# Revit family: Котел_ТЕРМОТЕХНИК_ТТ150_ 1000-20000 кВт
name_source: partatom
category: Оборудование
units: mm (PartAtom-declared; Revit-internal decimal feet)

## family parameters
Всегда вертикально = Да
Классификация = Нет
На основе рабочей плоскости = Нет
Общий = Нет
При загрузке вырезать с полостями = Нет
Размер круглого соединителя = Использовать диаметр
Тип детали = Нормальный
Точка расчета площади = Нет

## types (23) — shared parameters
G = 25 мм
URL = https://www.entroros.ru
Видимость_ВКЛ = Да
Видимость_ВЫКЛ = Нет
Изготовитель = ЭНТРОРОС
Ключевая пометка = https://www.entroros.ru
Код по классификатору = D3020100
Материал_Условный BOX = <По категории>
Описание = Котел ЭНТРОРОС ТЕРМОТЕХНИК ТТ150
Производитель = ЭНТРОРОС
Семейство заказано = ООО ЭНТРОРОС (entroros.ru)
Семейство оборудования = ТТ150
Семейство разработано = ООО DASBIM (dasbim.ru)
Ссылка на документацию = https://www.entroros.ru
Штуцер_Датчик дым.газов_D = G1/2-B
Штуцер_Датчик темп. воды на входе_D = G1/2-B
Штуцер_Датчик темп. воды на выходе_D = G1/2-B
Штуцер_Слив воды_D = 40 мм
Штуцер_Слив конденсата_D = 25 мм
Штуцер_Слив конденсата_D_Формула = G1-B
Штуцер_Тягонапоромер_D = G1/2-B
Эксплуатационный КПД (%) не менее = 94
zero-valued in all types: Стоимость

## per-type parameters (varying)
- 01_1000_ef_306: B=1540 мм; H=1768 мм; L=3183 мм; А_Горелка=135 мм; А_Дверь_Смещение наружной грани=3038 мм; Аэродин. сопротивление (Па)=256; Дверь_052=Нет; Дверь_053=Нет; Дверь_054=Нет; Дверь_055=Нет; Дверь_151=Нет; Дверь_206=Да; Дверь_208=Нет; Дверь_210=Нет; Дверь_212=Нет; Дверь_213=Нет; Комментарии к типоразмеру=1000 кВт; Корпус_054=Нет; Корпус_151=Нет; Корпус_306=Да; Корпус_310=Нет; Корпус_311=Нет; Корпус_312=Нет; Корпус_313=Нет; Корпус_361=Нет; Корпус_362=Нет; Корпус_366=Нет; Корпус_367=Нет; Корпус_408=Нет; Корпус_409=Нет; Масса наполненного котла (кг)=5030; Масса сухого котла (кг)=3476; Ном. мощность (кВт)=1000; Подключение горелки=300; С_Ось котла=910 мм; Штуцер_Вход воды_D=125 мм; Штуцер_Вход воды_А=400 мм; Штуцер_Выход воды_D=125 мм; Штуцер_Выход воды_А=1038 мм; Штуцер_Выход дыма_D=350 мм; Штуцер_Выход дыма_В=1360 мм; Штуцер_Подключение горелки=300 мм; Штуцер_Пред.клапан1_А=430 мм; Штуцер_Пред.клапан2_А=300 мм; Штуцер_Пред.клапан_D=50 мм; Штуцер_Слив воды_D_Формула=G1/2-B; Штуцер_Слив воды_А=0 мм; Штуцер_Слив воды_В=86 мм; Штуцер_Слив конденсата_А=0 мм; Штуцер_Слив конденсата_В=231 мм
- 02_1500_ef_307: B=1540 мм; H=1768 мм; L=3183 мм; А_Горелка=135 мм; А_Дверь_Смещение наружной грани=3038 мм; Аэродин. сопротивление (Па)=673; Дверь_052=Нет; Дверь_053=Нет; Дверь_054=Нет; Дверь_055=Нет; Дверь_151=Нет; Дверь_206=Да; Дверь_208=Нет; Дверь_210=Нет; Дверь_212=Нет; Дверь_213=Нет; Комментарии к типоразмеру=1500 кВт; Корпус_054=Нет; Корпус_151=Нет; Корпус_306=Да; Корпус_310=Нет; Корпус_311=Нет; Корпус_312=Нет; Корпус_313=Нет; Корпус_361=Нет; Корпус_362=Нет; Корпус_366=Нет; Корпус_367=Нет; Корпус_408=Нет; Корпус_409=Нет; Масса наполненного котла (кг)=5163; Масса сухого котла (кг)=3547; Ном. мощность (кВт)=1500; Подключение горелки=300; С_Ось котла=910 мм; Штуцер_Вход воды_D=125 мм; Штуцер_Вход воды_А=400 мм; Штуцер_Выход воды_D=125 мм; Штуцер_Выход воды_А=1038 мм; Штуцер_Выход дыма_D=350 мм; Штуцер_Выход дыма_В=1360 мм; Штуцер_Подключение горелки=300 мм; Штуцер_Пред.клапан1_А=430 мм; Штуцер_Пред.клапан2_А=300 мм; Штуцер_Пред.клапан_D=50 мм; Штуцер_Слив воды_D_Формула=G1/2-B; Штуцер_Слив воды_А=0 мм; Штуцер_Слив воды_В=86 мм; Штуцер_Слив конденсата_А=0 мм; Штуцер_Слив конденсата_В=231 мм
- 03_2000_ef_308: B=1740 мм; H=1968 мм; L=3485 мм; А_Горелка=135 мм; А_Дверь_Смещение наружной грани=3340 мм; Аэродин. сопротивление (Па)=832; Дверь_052=Нет; Дверь_053=Нет; Дверь_054=Нет; Дверь_055=Нет; Дверь_151=Нет; Дверь_206=Нет; Дверь_208=Да; Дверь_210=Нет; Дверь_212=Нет; Дверь_213=Нет; Комментарии к типоразмеру=2000 кВт; Корпус_054=Нет; Корпус_151=Нет; Корпус_306=Нет; Корпус_310=Нет; Корпус_311=Нет; Корпус_312=Нет; Корпус_313=Нет; Корпус_361=Нет; Корпус_362=Нет; Корпус_366=Нет; Корпус_367=Нет; Корпус_408=Да; Корпус_409=Нет; Масса наполненного котла (кг)=7070; Масса сухого котла (кг)=4976; Ном. мощность (кВт)=2000; Подключение горелки=380; С_Ось котла=1010 мм; Штуцер_Вход воды_D=150 мм; Штуцер_Вход воды_А=550 мм; Штуцер_Выход воды_D=150 мм; Штуцер_Выход воды_А=820 мм; Штуцер_Выход дыма_D=500 мм; Штуцер_Выход дыма_В=1520 мм; Штуцер_Подключение горелки=380 мм; Штуцер_Пред.клапан1_А=1205 мм; Штуцер_Пред.клапан2_А=300 мм; Штуцер_Пред.клапан_D=65 мм; Штуцер_Слив воды_D_Формула=G1/2-B; Штуцер_Слив воды_А=0 мм; Штуцер_Слив воды_В=86 мм; Штуцер_Слив конденсата_А=0 мм; Штуцер_Слив конденсата_В=232 мм
- 04_2200_ef_3081: B=1740 мм; H=1968 мм; L=3485 мм; А_Горелка=135 мм; А_Дверь_Смещение наружной грани=3340 мм; Аэродин. сопротивление (Па)=1043; Дверь_052=Нет; Дверь_053=Нет; Дверь_054=Нет; Дверь_055=Нет; Дверь_151=Нет; Дверь_206=Нет; Дверь_208=Да; Дверь_210=Нет; Дверь_212=Нет; Дверь_213=Нет; Комментарии к типоразмеру=2200 кВт; Корпус_054=Нет; Корпус_151=Нет; Корпус_306=Нет; Корпус_310=Нет; Корпус_311=Нет; Корпус_312=Нет; Корпус_313=Нет; Корпус_361=Нет; Корпус_362=Нет; Корпус_366=Нет; Корпус_367=Нет; Корпус_408=Да; Корпус_409=Нет; Масса наполненного котла (кг)=7249; Масса сухого котла (кг)=5078; Ном. мощность (кВт)=2200; Подключение горелки=380; С_Ось котла=1010 мм; Штуцер_Вход воды_D=150 мм; Штуцер_Вход воды_А=550 мм; Штуцер_Выход воды_D=150 мм; Штуцер_Выход воды_А=820 мм; Штуцер_Выход дыма_D=500 мм; Штуцер_Выход дыма_В=1520 мм; Штуцер_Подключение горелки=380 мм; Штуцер_Пред.клапан1_А=1205 мм; Штуцер_Пред.клапан2_А=300 мм; Штуцер_Пред.клапан_D=65 мм; Штуцер_Слив воды_D_Формула=G1/2-B; Штуцер_Слив воды_А=0 мм; Штуцер_Слив воды_В=86 мм; Штуцер_Слив конденсата_А=0 мм; Штуцер_Слив конденсата_В=232 мм
- 05_2500_ef_309: B=1740 мм; H=1968 мм; L=3735 мм; А_Горелка=135 мм; А_Дверь_Смещение наружной грани=3590 мм; Аэродин. сопротивление (Па)=1032; Дверь_052=Нет; Дверь_053=Нет; Дверь_054=Нет; Дверь_055=Нет; Дверь_151=Нет; Дверь_206=Нет; Дверь_208=Да; Дверь_210=Нет; Дверь_212=Нет; Дверь_213=Нет; Комментарии к типоразмеру=2500 кВт; Корпус_054=Нет; Корпус_151=Нет; Корпус_306=Нет; Корпус_310=Нет; Корпус_311=Нет; Корпус_312=Нет; Корпус_313=Нет; Корпус_361=Нет; Корпус_362=Нет; Корпус_366=Нет; Корпус_367=Нет; Корпус_408=Нет; Корпус_409=Да; Масса наполненного котла (кг)=7796; Масса сухого котла (кг)=5571; Ном. мощность (кВт)=2500; Подключение горелки=380; С_Ось котла=1010 мм; Штуцер_Вход воды_D=150 мм; Штуцер_Вход воды_А=550 мм; Штуцер_Выход воды_D=150 мм; Штуцер_Выход воды_А=875 мм; Штуцер_Выход дыма_D=500 мм; Штуцер_Выход дыма_В=1520 мм; Штуцер_Подключение горелки=380 мм; Штуцер_Пред.клапан1_А=1400 мм; Штуцер_Пред.клапан2_А=300 мм; Штуцер_Пред.клапан_D=65 мм; Штуцер_Слив воды_D_Формула=G1/2-B; Штуцер_Слив воды_А=0 мм; Штуцер_Слив воды_В=89 мм; Штуцер_Слив конденсата_А=0 мм; Штуцер_Слив конденсата_В=233 мм
- 06_3000_ef_310: B=1940 мм; H=2168 мм; L=4123 мм; А_Горелка=135 мм; А_Дверь_Смещение наружной грани=3978 мм; Аэродин. сопротивление (Па)=898; Дверь_052=Нет; Дверь_053=Нет; Дверь_054=Нет; Дверь_055=Нет; Дверь_151=Нет; Дверь_206=Нет; Дверь_208=Нет; Дверь_210=Да; Дверь_212=Нет; Дверь_213=Нет; Комментарии к типоразмеру=3000 кВт; Корпус_054=Нет; Корпус_151=Нет; Корпус_306=Нет; Корпус_310=Да; Корпус_311=Нет; Корпус_312=Нет; Корпус_313=Нет; Корпус_361=Нет; Корпус_362=Нет; Корпус_366=Нет; Корпус_367=Нет; Корпус_408=Нет; Корпус_409=Нет; Масса наполненного котла (кг)=10357; Масса сухого котла (кг)=7423; Ном. мощность (кВт)=3000; Подключение горелки=450; С_Ось котла=1110 мм; Штуцер_Вход воды_D=200 мм; Штуцер_Вход воды_А=600 мм; Штуцер_Выход воды_D=200 мм; Штуцер_Выход воды_А=963 мм; Штуцер_Выход дыма_D=500 мм; Штуцер_Выход дыма_В=1720 мм; Штуцер_Подключение горелки=450 мм; Штуцер_Пред.клапан1_А=1600 мм; Штуцер_Пред.клапан2_А=300 мм; Штуцер_Пред.клапан_D=65 мм; Штуцер_Слив воды_D_Формула=G1/2-B; Штуцер_Слив воды_А=0 мм; Штуцер_Слив воды_В=86 мм; Штуцер_Слив конденсата_А=0 мм; Штуцер_Слив конденсата_В=233 мм
- 07_3200_ef_3101: B=1940 мм; H=2168 мм; L=4123 мм; А_Горелка=135 мм; А_Дверь_Смещение наружной грани=3978 мм; Аэродин. сопротивление (Па)=1046; Дверь_052=Нет; Дверь_053=Нет; Дверь_054=Нет; Дверь_055=Нет; Дверь_151=Нет; Дверь_206=Нет; Дверь_208=Нет; Дверь_210=Да; Дверь_212=Нет; Дверь_213=Нет; Комментарии к типоразмеру=3200 кВт; Корпус_054=Нет; Корпус_151=Нет; Корпус_306=Нет; Корпус_310=Да; Корпус_311=Нет; Корпус_312=Нет; Корпус_313=Нет; Корпус_361=Нет; Корпус_362=Нет; Корпус_366=Нет; Корпус_367=Нет; Корпус_408=Нет; Корпус_409=Нет; Масса наполненного котла (кг)=10625; Масса сухого котла (кг)=7575; Ном. мощность (кВт)=3200; Подключение горелки=450; С_Ось котла=1110 мм; Штуцер_Вход воды_D=200 мм; Штуцер_Вход воды_А=600 мм; Штуцер_Выход воды_D=200 мм; Штуцер_Выход воды_А=963 мм; Штуцер_Выход дыма_D=500 мм; Штуцер_Выход дыма_В=1720 мм; Штуцер_Подключение горелки=450 мм; Штуцер_Пред.клапан1_А=1600 мм; Штуцер_Пред.клапан2_А=300 мм; Штуцер_Пред.клапан_D=65 мм; Штуцер_Слив воды_D_Формула=G1/2-B; Штуцер_Слив воды_А=0 мм; Штуцер_Слив воды_В=86 мм; Штуцер_Слив конденсата_А=0 мм; Штуцер_Слив конденсата_В=233 мм
- 08_3500_ef_311: B=1940 мм; H=2168 мм; L=4523 мм; А_Горелка=135 мм; А_Дверь_Смещение наружной грани=4378 мм; Аэродин. сопротивление (Па)=1245; Дверь_052=Нет; Дверь_053=Нет; Дверь_054=Нет; Дверь_055=Нет; Дверь_151=Нет; Дверь_206=Нет; Дверь_208=Нет; Дверь_210=Да; Дверь_212=Нет; Дверь_213=Нет; Комментарии к типоразмеру=3500 кВт; Корпус_054=Нет; Корпус_151=Нет; Корпус_306=Нет; Корпус_310=Нет; Корпус_311=Да; Корпус_312=Нет; Корпус_313=Нет; Корпус_361=Нет; Корпус_362=Нет; Корпус_366=Нет; Корпус_367=Нет; Корпус_408=Нет; Корпус_409=Нет; Масса наполненного котла (кг)=11714; Масса сухого котла (кг)=8246; Ном. мощность (кВт)=3500; Подключение горелки=450; С_Ось котла=1110 мм; Штуцер_Вход воды_D=200 мм; Штуцер_Вход воды_А=600 мм; Штуцер_Выход воды_D=200 мм; Штуцер_Выход воды_А=1013 мм; Штуцер_Выход дыма_D=500 мм; Штуцер_Выход дыма_В=1720 мм; Штуцер_Подключение горелки=450 мм; Штуцер_Пред.клапан1_А=1950 мм; Штуцер_Пред.клапан2_А=300 мм; Штуцер_Пред.клапан_D=65 мм; Штуцер_Слив воды_D_Формула=G1/2-B; Штуцер_Слив воды_А=0 мм; Штуцер_Слив воды_В=86 мм; Штуцер_Слив конденсата_А=0 мм; Штуцер_Слив конденсата_В=233 мм
- 09_4200_ef_312: B=2100 мм; H=2326 мм; L=4820 мм; А_Горелка=135 мм; А_Дверь_Смещение наружной грани=4675 мм; Аэродин. сопротивление (Па)=1213; Дверь_052=Нет; Дверь_053=Нет; Дверь_054=Нет; Дверь_055=Нет; Дверь_151=Нет; Дверь_206=Нет; Дверь_208=Нет; Дверь_210=Нет; Дверь_212=Да; Дверь_213=Нет; Комментарии к типоразмеру=4200 кВт; Корпус_054=Нет; Корпус_151=Нет; Корпус_306=Нет; Корпус_310=Нет; Корпус_311=Нет; Корпус_312=Да; Корпус_313=Нет; Корпус_361=Нет; Корпус_362=Нет; Корпус_366=Нет; Корпус_367=Нет; Корпус_408=Нет; Корпус_409=Нет; Масса наполненного котла (кг)=14037; Масса сухого котла (кг)=10222; Ном. мощность (кВт)=4200; Подключение горелки=450; С_Ось котла=1205 мм; Штуцер_Вход воды_D=200 мм; Штуцер_Вход воды_А=700 мм; Штуцер_Выход воды_D=200 мм; Штуцер_Выход воды_А=960 мм; Штуцер_Выход дыма_D=650 мм; Штуцер_Выход дыма_В=1805 мм; Штуцер_Подключение горелки=450 мм; Штуцер_Пред.клапан1_А=2100 мм; Штуцер_Пред.клапан2_А=300 мм; Штуцер_Пред.клапан_D=80 мм; Штуцер_Слив воды_D_Формула=G1/2-B; Штуцер_Слив воды_А=0 мм; Штуцер_Слив воды_В=121 мм; Штуцер_Слив конденсата_А=0 мм; Штуцер_Слив конденсата_В=265 мм
- 10_5000_ef_3121: B=2100 мм; H=2326 мм; L=4820 мм; А_Горелка=135 мм; А_Дверь_Смещение наружной грани=4675 мм; Аэродин. сопротивление (Па)=1806; Дверь_052=Нет; Дверь_053=Нет; Дверь_054=Нет; Дверь_055=Нет; Дверь_151=Нет; Дверь_206=Нет; Дверь_208=Нет; Дверь_210=Нет; Дверь_212=Да; Дверь_213=Нет; Комментарии к типоразмеру=5000 кВт; Корпус_054=Нет; Корпус_151=Нет; Корпус_306=Нет; Корпус_310=Нет; Корпус_311=Нет; Корпус_312=Да; Корпус_313=Нет; Корпус_361=Нет; Корпус_362=Нет; Корпус_366=Нет; Корпус_367=Нет; Корпус_408=Нет; Корпус_409=Нет; Масса наполненного котла (кг)=14405; Масса сухого котла (кг)=10431; Ном. мощность (кВт)=5000; Подключение горелки=450; С_Ось котла=1205 мм; Штуцер_Вход воды_D=200 мм; Штуцер_Вход воды_А=700 мм; Штуцер_Выход воды_D=200 мм; Штуцер_Выход воды_А=960 мм; Штуцер_Выход дыма_D=650 мм; Штуцер_Выход дыма_В=1805 мм; Штуцер_Подключение горелки=450 мм; Штуцер_Пред.клапан1_А=2100 мм; Штуцер_Пред.клапан2_А=300 мм; Штуцер_Пред.клапан_D=80 мм; Штуцер_Слив воды_D_Формула=G1/2-B; Штуцер_Слив воды_А=0 мм; Штуцер_Слив воды_В=121 мм; Штуцер_Слив конденсата_А=0 мм; Штуцер_Слив конденсата_В=265 мм
- 11_5400_ef_313: B=2200 мм; H=2436 мм; L=5109 мм; А_Горелка=135 мм; А_Дверь_Смещение наружной грани=4964 мм; Аэродин. сопротивление (Па)=1059; Дверь_052=Нет; Дверь_053=Нет; Дверь_054=Нет; Дверь_055=Нет; Дверь_151=Нет; Дверь_206=Нет; Дверь_208=Нет; Дверь_210=Нет; Дверь_212=Нет; Дверь_213=Да; Комментарии к типоразмеру=5400 кВт; Корпус_054=Нет; Корпус_151=Нет; Корпус_306=Нет; Корпус_310=Нет; Корпус_311=Нет; Корпус_312=Нет; Корпус_313=Да; Корпус_361=Нет; Корпус_362=Нет; Корпус_366=Нет; Корпус_367=Нет; Корпус_408=Нет; Корпус_409=Нет; Масса наполненного котла (кг)=16565; Масса сухого котла (кг)=11363; Ном. мощность (кВт)=5400; Подключение горелки=450; С_Ось котла=1260 мм; Штуцер_Вход воды_D=250 мм; Штуцер_Вход воды_А=800 мм; Штуцер_Выход воды_D=250 мм; Штуцер_Выход воды_А=1147 мм; Штуцер_Выход дыма_D=650 мм; Штуцер_Выход дыма_В=1888 мм; Штуцер_Подключение горелки=450 мм; Штуцер_Пред.клапан1_А=2100 мм; Штуцер_Пред.клапан2_А=300 мм; Штуцер_Пред.клапан_D=80 мм; Штуцер_Слив воды_D_Формула=G1/2-B; Штуцер_Слив воды_А=0 мм; Штуцер_Слив воды_В=139 мм; Штуцер_Слив конденсата_А=0 мм; Штуцер_Слив конденсата_В=261 мм
- 12_6000_ef_3131: B=2200 мм; H=2436 мм; L=5109 мм; А_Горелка=135 мм; А_Дверь_Смещение наружной грани=4964 мм; Аэродин. сопротивление (Па)=1353; Дверь_052=Нет; Дверь_053=Нет; Дверь_054=Нет; Дверь_055=Нет; Дверь_151=Нет; Дверь_206=Нет; Дверь_208=Нет; Дверь_210=Нет; Дверь_212=Нет; Дверь_213=Да; Комментарии к типоразмеру=6000 кВт; Корпус_054=Нет; Корпус_151=Нет; Корпус_306=Нет; Корпус_310=Нет; Корпус_311=Нет; Корпус_312=Нет; Корпус_313=Да; Корпус_361=Нет; Корпус_362=Нет; Корпус_366=Нет; Корпус_367=Нет; Корпус_408=Нет; Корпус_409=Нет; Масса наполненного котла (кг)=16999; Масса сухого котла (кг)=11595; Ном. мощность (кВт)=6000; Подключение горелки=450; С_Ось котла=1260 мм; Штуцер_Вход воды_D=250 мм; Штуцер_Вход воды_А=800 мм; Штуцер_Выход воды_D=250 мм; Штуцер_Выход воды_А=1147 мм; Штуцер_Выход дыма_D=650 мм; Штуцер_Выход дыма_В=1888 мм; Штуцер_Подключение горелки=450 мм; Штуцер_Пред.клапан1_А=2100 мм; Штуцер_Пред.клапан2_А=300 мм; Штуцер_Пред.клапан_D=80 мм; Штуцер_Слив воды_D_Формула=50; Штуцер_Слив воды_А=0 мм; Штуцер_Слив воды_В=139 мм; Штуцер_Слив конденсата_А=0 мм; Штуцер_Слив конденсата_В=261 мм
- 13_6500_ef_151: B=2352 мм; H=2576 мм; L=5394 мм; А_Горелка=135 мм; А_Дверь_Смещение наружной грани=5249 мм; Аэродин. сопротивление (Па)=1126; Дверь_052=Нет; Дверь_053=Нет; Дверь_054=Нет; Дверь_055=Нет; Дверь_151=Да; Дверь_206=Нет; Дверь_208=Нет; Дверь_210=Нет; Дверь_212=Нет; Дверь_213=Нет; Комментарии к типоразмеру=6500 кВт; Корпус_054=Нет; Корпус_151=Да; Корпус_306=Нет; Корпус_310=Нет; Корпус_311=Нет; Корпус_312=Нет; Корпус_313=Нет; Корпус_361=Нет; Корпус_362=Нет; Корпус_366=Нет; Корпус_367=Нет; Корпус_408=Нет; Корпус_409=Нет; Масса наполненного котла (кг)=20128; Масса сухого котла (кг)=14706; Ном. мощность (кВт)=6500; Подключение горелки=500; С_Ось котла=1314 мм; Штуцер_Вход воды_D=250 мм; Штуцер_Вход воды_А=900 мм; Штуцер_Выход воды_D=250 мм; Штуцер_Выход воды_А=1134 мм; Штуцер_Выход дыма_D=800 мм; Штуцер_Выход дыма_В=1970 мм; Штуцер_Подключение горелки=500 мм; Штуцер_Пред.клапан1_А=1970 мм; Штуцер_Пред.клапан2_А=470 мм; Штуцер_Пред.клапан_D=100 мм; Штуцер_Слив воды_D_Формула=50; Штуцер_Слив воды_А=0 мм; Штуцер_Слив воды_В=110 мм; Штуцер_Слив конденсата_А=0 мм; Штуцер_Слив конденсата_В=237 мм
- 14_7000_ef_1511: B=2352 мм; H=2576 мм; L=5394 мм; А_Горелка=135 мм; А_Дверь_Смещение наружной грани=5249 мм; Аэродин. сопротивление (Па)=1339; Дверь_052=Нет; Дверь_053=Нет; Дверь_054=Нет; Дверь_055=Нет; Дверь_151=Да; Дверь_206=Нет; Дверь_208=Нет; Дверь_210=Нет; Дверь_212=Нет; Дверь_213=Нет; Комментарии к типоразмеру=7000 кВт; Корпус_054=Нет; Корпус_151=Да; Корпус_306=Нет; Корпус_310=Нет; Корпус_311=Нет; Корпус_312=Нет; Корпус_313=Нет; Корпус_361=Нет; Корпус_362=Нет; Корпус_366=Нет; Корпус_367=Нет; Корпус_408=Нет; Корпус_409=Нет; Масса наполненного котла (кг)=20671; Масса сухого котла (кг)=15007; Ном. мощность (кВт)=7000; Подключение горелки=500; С_Ось котла=1314 мм; Штуцер_Вход воды_D=250 мм; Штуцер_Вход воды_А=900 мм; Штуцер_Выход воды_D=250 мм; Штуцер_Выход воды_А=1134 мм; Штуцер_Выход дыма_D=800 мм; Штуцер_Выход дыма_В=1790 мм; Штуцер_Подключение горелки=500 мм; Штуцер_Пред.клапан1_А=1970 мм; Штуцер_Пред.клапан2_А=470 мм; Штуцер_Пред.клапан_D=100 мм; Штуцер_Слив воды_D_Формула=50; Штуцер_Слив воды_А=0 мм; Штуцер_Слив воды_В=110 мм; Штуцер_Слив конденсата_А=0 мм; Штуцер_Слив конденсата_В=237 мм
- 15_8000_ef_361: B=2500 мм; H=2710 мм; L=5806 мм; А_Горелка=148 мм; А_Дверь_Смещение наружной грани=5648 мм; Аэродин. сопротивление (Па)=1255; Дверь_052=Да; Дверь_053=Нет; Дверь_054=Нет; Дверь_055=Нет; Дверь_151=Нет; Дверь_206=Нет; Дверь_208=Нет; Дверь_210=Нет; Дверь_212=Нет; Дверь_213=Нет; Комментарии к типоразмеру=8000 кВт; Корпус_054=Нет; Корпус_151=Нет; Корпус_306=Нет; Корпус_310=Нет; Корпус_311=Нет; Корпус_312=Нет; Корпус_313=Нет; Корпус_361=Да; Корпус_362=Нет; Корпус_366=Нет; Корпус_367=Нет; Корпус_408=Нет; Корпус_409=Нет; Масса наполненного котла (кг)=24720; Масса сухого котла (кг)=17727; Ном. мощность (кВт)=8000; Подключение горелки=590; С_Ось котла=1370 мм; Штуцер_Вход воды_D=300 мм; Штуцер_Вход воды_А=1000 мм; Штуцер_Выход воды_D=300 мм; Штуцер_Выход воды_А=1216 мм; Штуцер_Выход дыма_D=800 мм; Штуцер_Выход дыма_В=2070 мм; Штуцер_Подключение горелки=590 мм; Штуцер_Пред.клапан1_А=1990 мм; Штуцер_Пред.клапан2_А=500 мм; Штуцер_Пред.клапан_D=100 мм; Штуцер_Слив воды_D_Формула=50; Штуцер_Слив воды_А=0 мм; Штуцер_Слив воды_В=99 мм; Штуцер_Слив конденсата_А=0 мм; Штуцер_Слив конденсата_В=213 мм
- 16_8700_ef_3611: B=2500 мм; H=2710 мм; L=5806 мм; А_Горелка=148 мм; А_Дверь_Смещение наружной грани=5648 мм; Аэродин. сопротивление (Па)=1524; Дверь_052=Да; Дверь_053=Нет; Дверь_054=Нет; Дверь_055=Нет; Дверь_151=Нет; Дверь_206=Нет; Дверь_208=Нет; Дверь_210=Нет; Дверь_212=Нет; Дверь_213=Нет; Комментарии к типоразмеру=8700 кВт; Корпус_054=Нет; Корпус_151=Нет; Корпус_306=Нет; Корпус_310=Нет; Корпус_311=Нет; Корпус_312=Нет; Корпус_313=Нет; Корпус_361=Да; Корпус_362=Нет; Корпус_366=Нет; Корпус_367=Нет; Корпус_408=Нет; Корпус_409=Нет; Масса наполненного котла (кг)=25373; Масса сухого котла (кг)=18089; Ном. мощность (кВт)=8700; Подключение горелки=590; С_Ось котла=1370 мм; Штуцер_Вход воды_D=300 мм; Штуцер_Вход воды_А=1000 мм; Штуцер_Выход воды_D=300 мм; Штуцер_Выход воды_А=1216 мм; Штуцер_Выход дыма_D=800 мм; Штуцер_Выход дыма_В=2070 мм; Штуцер_Подключение горелки=590 мм; Штуцер_Пред.клапан1_А=1990 мм; Штуцер_Пред.клапан2_А=500 мм; Штуцер_Пред.клапан_D=100 мм; Штуцер_Слив воды_D_Формула=50; Штуцер_Слив воды_А=0 мм; Штуцер_Слив воды_В=99 мм; Штуцер_Слив конденсата_А=0 мм; Штуцер_Слив конденсата_В=213 мм
- 17_10000_ef_362: B=2680 мм; H=2862 мм; L=6442 мм; А_Горелка=142 мм; А_Дверь_Смещение наружной грани=6290 мм; Аэродин. сопротивление (Па)=1458; Дверь_052=Нет; Дверь_053=Да; Дверь_054=Нет; Дверь_055=Нет; Дверь_151=Нет; Дверь_206=Нет; Дверь_208=Нет; Дверь_210=Нет; Дверь_212=Нет; Дверь_213=Нет; Комментарии к типоразмеру=10000 кВт; Корпус_054=Нет; Корпус_151=Нет; Корпус_306=Нет; Корпус_310=Нет; Корпус_311=Нет; Корпус_312=Нет; Корпус_313=Нет; Корпус_361=Нет; Корпус_362=Да; Корпус_366=Нет; Корпус_367=Нет; Корпус_408=Нет; Корпус_409=Нет; Масса наполненного котла (кг)=30251; Масса сухого котла (кг)=21119; Ном. мощность (кВт)=10000; Подключение горелки=590; С_Ось котла=1450 мм; Штуцер_Вход воды_D=300 мм; Штуцер_Вход воды_А=1400 мм; Штуцер_Выход воды_D=300 мм; Штуцер_Выход воды_А=1228 мм; Штуцер_Выход дыма_D=900 мм; Штуцер_Выход дыма_В=2130 мм; Штуцер_Подключение горелки=590 мм; Штуцер_Пред.клапан1_А=2350 мм; Штуцер_Пред.клапан2_А=500 мм; Штуцер_Пред.клапан_D=125 мм; Штуцер_Слив воды_D_Формула=50; Штуцер_Слив воды_А=24 мм; Штуцер_Слив воды_В=139 мм; Штуцер_Слив конденсата_А=25 мм; Штуцер_Слив конденсата_В=261 мм
- 18_12000_ef_363: B=2860 мм; H=3074 мм; L=6950 мм; А_Горелка=135 мм; А_Дверь_Смещение наружной грани=6805 мм; Аэродин. сопротивление (Па)=1482; Дверь_052=Нет; Дверь_053=Нет; Дверь_054=Да; Дверь_055=Нет; Дверь_151=Нет; Дверь_206=Нет; Дверь_208=Нет; Дверь_210=Нет; Дверь_212=Нет; Дверь_213=Нет; Комментарии к типоразмеру=12000 кВт; Корпус_054=Да; Корпус_151=Нет; Корпус_306=Нет; Корпус_310=Нет; Корпус_311=Нет; Корпус_312=Нет; Корпус_313=Нет; Корпус_361=Нет; Корпус_362=Нет; Корпус_366=Нет; Корпус_367=Нет; Корпус_408=Нет; Корпус_409=Нет; Масса наполненного котла (кг)=34848; Масса сухого котла (кг)=24988; Ном. мощность (кВт)=12000; Подключение горелки=730; С_Ось котла=1564 мм; Штуцер_Вход воды_D=350 мм; Штуцер_Вход воды_А=1600 мм; Штуцер_Выход воды_D=350 мм; Штуцер_Выход воды_А=1506 мм; Штуцер_Выход дыма_D=1000 мм; Штуцер_Выход дыма_В=2364 мм; Штуцер_Подключение горелки=730 мм; Штуцер_Пред.клапан1_А=2440 мм; Штуцер_Пред.клапан2_А=500 мм; Штуцер_Пред.клапан_D=125 мм; Штуцер_Слив воды_D_Формула=50; Штуцер_Слив воды_А=0 мм; Штуцер_Слив воды_В=109 мм; Штуцер_Слив конденсата_А=86 мм; Штуцер_Слив конденсата_В=261 мм
- 19_13000_ef_364: B=2860 мм; H=3074 мм; L=6950 мм; А_Горелка=135 мм; А_Дверь_Смещение наружной грани=6805 мм; Аэродин. сопротивление (Па)=1790; Дверь_052=Нет; Дверь_053=Нет; Дверь_054=Да; Дверь_055=Нет; Дверь_151=Нет; Дверь_206=Нет; Дверь_208=Нет; Дверь_210=Нет; Дверь_212=Нет; Дверь_213=Нет; Комментарии к типоразмеру=13000 кВт; Корпус_054=Да; Корпус_151=Нет; Корпус_306=Нет; Корпус_310=Нет; Корпус_311=Нет; Корпус_312=Нет; Корпус_313=Нет; Корпус_361=Нет; Корпус_362=Нет; Корпус_366=Нет; Корпус_367=Нет; Корпус_408=Нет; Корпус_409=Нет; Масса наполненного котла (кг)=35709; Масса сухого котла (кг)=25498; Ном. мощность (кВт)=13000; Подключение горелки=730; С_Ось котла=1564 мм; Штуцер_Вход воды_D=350 мм; Штуцер_Вход воды_А=1600 мм; Штуцер_Выход воды_D=350 мм; Штуцер_Выход воды_А=1506 мм; Штуцер_Выход дыма_D=1000 мм; Штуцер_Выход дыма_В=2364 мм; Штуцер_Подключение горелки=730 мм; Штуцер_Пред.клапан1_А=2440 мм; Штуцер_Пред.клапан2_А=500 мм; Штуцер_Пред.клапан_D=125 мм; Штуцер_Слив воды_D_Формула=50; Штуцер_Слив воды_А=0 мм; Штуцер_Слив воды_В=109 мм; Штуцер_Слив конденсата_А=86 мм; Штуцер_Слив конденсата_В=227 мм
- 20_15000_ef_366: B=3060 мм; H=3276 мм; L=7608 мм; А_Горелка=137 мм; А_Дверь_Смещение наружной грани=7461 мм; Аэродин. сопротивление (Па)=1798; Дверь_052=Нет; Дверь_053=Нет; Дверь_054=Нет; Дверь_055=Да; Дверь_151=Нет; Дверь_206=Нет; Дверь_208=Нет; Дверь_210=Нет; Дверь_212=Нет; Дверь_213=Нет; Комментарии к типоразмеру=15000 кВт; Корпус_054=Нет; Корпус_151=Нет; Корпус_306=Нет; Корпус_310=Нет; Корпус_311=Нет; Корпус_312=Нет; Корпус_313=Нет; Корпус_361=Нет; Корпус_362=Нет; Корпус_366=Да; Корпус_367=Нет; Корпус_408=Нет; Корпус_409=Нет; Масса наполненного котла (кг)=45191; Масса сухого котла (кг)=31167; Ном. мощность (кВт)=15000; Подключение горелки=730; С_Ось котла=1664 мм; Штуцер_Вход воды_D=400 мм; Штуцер_Вход воды_А=2000 мм; Штуцер_Выход воды_D=400 мм; Штуцер_Выход воды_А=1396 мм; Штуцер_Выход дыма_D=1000 мм; Штуцер_Выход дыма_В=2514 мм; Штуцер_Подключение горелки=730 мм; Штуцер_Пред.клапан1_А=2550 мм; Штуцер_Пред.клапан2_А=600 мм; Штуцер_Пред.клапан_D=125 мм; Штуцер_Слив воды_D_Формула=50; Штуцер_Слив воды_А=0 мм; Штуцер_Слив воды_В=113 мм; Штуцер_Слив конденсата_А=86 мм; Штуцер_Слив конденсата_В=230 мм
- 21_16500_ef_3661: B=3060 мм; H=3276 мм; L=7608 мм; А_Горелка=137 мм; А_Дверь_Смещение наружной грани=7461 мм; Аэродин. сопротивление (Па)=2239; Дверь_052=Нет; Дверь_053=Нет; Дверь_054=Нет; Дверь_055=Да; Дверь_151=Нет; Дверь_206=Нет; Дверь_208=Нет; Дверь_210=Нет; Дверь_212=Нет; Дверь_213=Нет; Комментарии к типоразмеру=16500 кВт; Корпус_054=Нет; Корпус_151=Нет; Корпус_306=Нет; Корпус_310=Нет; Корпус_311=Нет; Корпус_312=Нет; Корпус_313=Нет; Корпус_361=Нет; Корпус_362=Нет; Корпус_366=Да; Корпус_367=Нет; Корпус_408=Нет; Корпус_409=Нет; Масса наполненного котла (кг)=46306; Масса сухого котла (кг)=31804; Ном. мощность (кВт)=16500; Подключение горелки=730; С_Ось котла=1664 мм; Штуцер_Вход воды_D=400 мм; Штуцер_Вход воды_А=2000 мм; Штуцер_Выход воды_D=400 мм; Штуцер_Выход воды_А=1396 мм; Штуцер_Выход дыма_D=1000 мм; Штуцер_Выход дыма_В=2514 мм; Штуцер_Подключение горелки=730 мм; Штуцер_Пред.клапан1_А=2550 мм; Штуцер_Пред.клапан2_А=600 мм; Штуцер_Пред.клапан_D=125 мм; Штуцер_Слив воды_D_Формула=50; Штуцер_Слив воды_А=0 мм; Штуцер_Слив воды_В=113 мм; Штуцер_Слив конденсата_А=86 мм; Штуцер_Слив конденсата_В=230 мм
- 22_18000_ef_3671: B=3647 мм; H=3841 мм; L=8629 мм; А_Горелка=323 мм; А_Дверь_Смещение наружной грани=8636 мм; Аэродин. сопротивление (Па)=1344; Дверь_052=Нет; Дверь_053=Нет; Дверь_054=Нет; Дверь_055=Нет; Дверь_151=Нет; Дверь_206=Нет; Дверь_208=Нет; Дверь_210=Нет; Дверь_212=Нет; Дверь_213=Нет; Комментарии к типоразмеру=18000 кВт; Корпус_054=Нет; Корпус_151=Нет; Корпус_306=Нет; Корпус_310=Нет; Корпус_311=Нет; Корпус_312=Нет; Корпус_313=Нет; Корпус_361=Нет; Корпус_362=Нет; Корпус_366=Нет; Корпус_367=Да; Корпус_408=Нет; Корпус_409=Нет; Масса наполненного котла (кг)=63138; Масса сухого котла (кг)=40555; Ном. мощность (кВт)=18000; Подключение горелки=760; С_Ось котла=1400 мм; Штуцер_Вход воды_D=400 мм; Штуцер_Вход воды_А=1700 мм; Штуцер_Выход воды_D=400 мм; Штуцер_Выход воды_А=1754 мм; Штуцер_Выход дыма_D=1100 мм; Штуцер_Выход дыма_В=2800 мм; Штуцер_Подключение горелки=760 мм; Штуцер_Пред.клапан1_А=3120 мм; Штуцер_Пред.клапан2_А=750 мм; Штуцер_Пред.клапан_D=125 мм; Штуцер_Слив воды_D_Формула=50; Штуцер_Слив воды_А=292 мм; Штуцер_Слив воды_В=91 мм; Штуцер_Слив конденсата_А=292 мм; Штуцер_Слив конденсата_В=91 мм
- 23_20000_ef_367: B=3647 мм; H=3841 мм; L=8629 мм; А_Горелка=323 мм; А_Дверь_Смещение наружной грани=8636 мм; Аэродин. сопротивление (Па)=1712; Дверь_052=Нет; Дверь_053=Нет; Дверь_054=Нет; Дверь_055=Нет; Дверь_151=Нет; Дверь_206=Нет; Дверь_208=Нет; Дверь_210=Нет; Дверь_212=Нет; Дверь_213=Нет; Комментарии к типоразмеру=20000 кВт; Корпус_054=Нет; Корпус_151=Нет; Корпус_306=Нет; Корпус_310=Нет; Корпус_311=Нет; Корпус_312=Нет; Корпус_313=Нет; Корпус_361=Нет; Корпус_362=Нет; Корпус_366=Нет; Корпус_367=Да; Корпус_408=Нет; Корпус_409=Нет; Масса наполненного котла (кг)=64738; Масса сухого котла (кг)=41383; Ном. мощность (кВт)=20000; Подключение горелки=760; С_Ось котла=1400 мм; Штуцер_Вход воды_D=400 мм; Штуцер_Вход воды_А=1700 мм; Штуцер_Выход воды_D=400 мм; Штуцер_Выход воды_А=1754 мм; Штуцер_Выход дыма_D=1100 мм; Штуцер_Выход дыма_В=2800 мм; Штуцер_Подключение горелки=760 мм; Штуцер_Пред.клапан1_А=3120 мм; Штуцер_Пред.клапан2_А=750 мм; Штуцер_Пред.клапан_D=125 мм; Штуцер_Слив воды_D_Формула=50; Штуцер_Слив воды_А=292 мм; Штуцер_Слив воды_В=91 мм; Штуцер_Слив конденсата_А=292 мм; Штуцер_Слив конденсата_В=91 мм
